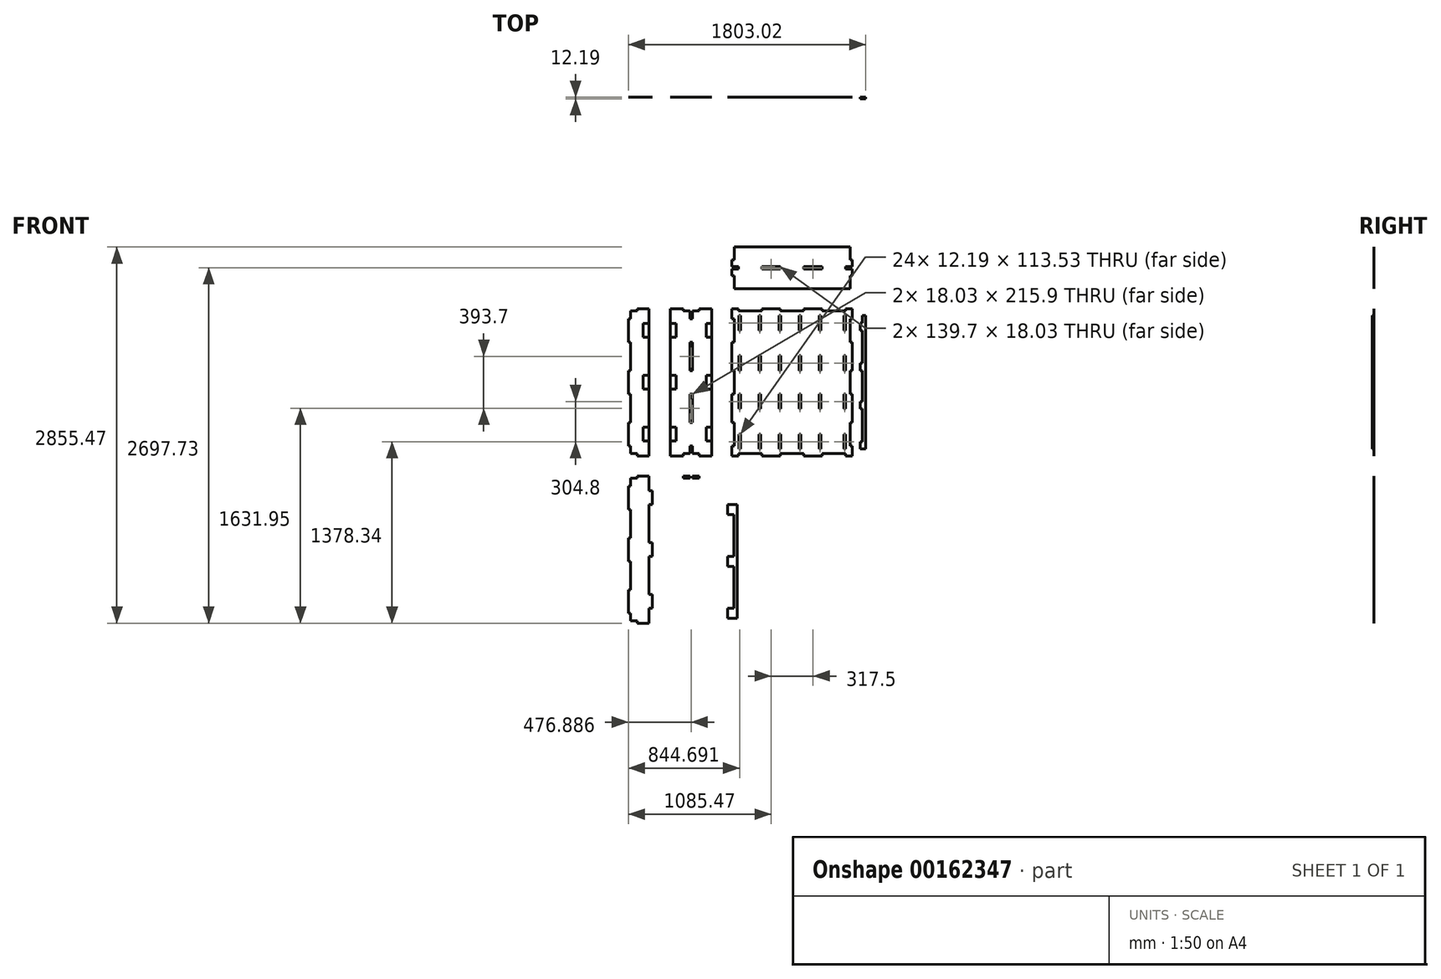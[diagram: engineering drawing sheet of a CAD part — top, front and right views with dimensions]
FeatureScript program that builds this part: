
annotation { "Feature Type Name" : "Feature", "Feature Type Description" : "" }
export const myFeature = defineFeature(function(context is Context, id is Id, definition is map)
    precondition{}
    {
        {
            assignVariable(context, id + "F0", {"name" : "ply34", "anyValue" : 0.71});
        }
        {
            var Q0;
            Q0=qCreatedBy(makeId("Front.planeOp"),FACE);
            var sketch = newSketch(context, id + "F1", { "sketchPlane" : qUnion([Q0])});
            skLineSegment(sketch, "E0.bottom", {"start": v(-457.2, 558.8) * mm, "end": v(457.2, 558.8) * mm});
            skLineSegment(sketch, "E0.top", {"start": v(-457.2, -558.8) * mm, "end": v(457.2, -558.8) * mm});
            skLineSegment(sketch, "E0.left", {"start": v(-457.2, 558.8) * mm, "end": v(-457.2, -558.8) * mm});
            skLineSegment(sketch, "E0.right", {"start": v(457.2, 558.8) * mm, "end": v(457.2, -558.8) * mm});
            skPoint(sketch, "E0.middle", {"position": v(0, 0) * mm});
            skLineSegment(sketch, "E1.bottom", {"start": v(-457.2, 482.6) * mm, "end": v(-439.17, 482.6) * mm});
            skLineSegment(sketch, "E1.top", {"start": v(-457.2, 304.8) * mm, "end": v(-439.17, 304.8) * mm});
            skLineSegment(sketch, "E1.left", {"start": v(-457.2, 482.6) * mm, "end": v(-457.2, 304.8) * mm});
            skLineSegment(sketch, "E1.right", {"start": v(-439.17, 482.6) * mm, "end": v(-439.17, 304.8) * mm});
            skLineSegment(sketch, "E2.bottom", {"start": v(-457.2, 88.9) * mm, "end": v(-439.17, 88.9) * mm});
            skLineSegment(sketch, "E2.top", {"start": v(-457.2, -88.9) * mm, "end": v(-439.17, -88.9) * mm});
            skLineSegment(sketch, "E2.left", {"start": v(-457.2, 88.9) * mm, "end": v(-457.2, -88.9) * mm});
            skLineSegment(sketch, "E2.right", {"start": v(-439.17, 88.9) * mm, "end": v(-439.17, -88.9) * mm});
            skPoint(sketch, "E3", {"position": v(-439.17, 0) * mm});
            skLineSegment(sketch, "E4", {"start": v(-457.2, 0) * mm, "end": v(457.2, 0) * mm, "construction": true});
            skLineSegment(sketch, "E5", {"start": v(0, 558.8) * mm, "end": v(0, -558.8) * mm, "construction": true});
            skLineSegment(sketch, "E6.MirrorCS", {"start": v(-457.2, -482.6) * mm, "end": v(-439.17, -482.6) * mm});
            skLineSegment(sketch, "E7.MirrorCS", {"start": v(-457.2, -304.8) * mm, "end": v(-439.17, -304.8) * mm});
            skLineSegment(sketch, "E8.MirrorCS", {"start": v(-457.2, -482.6) * mm, "end": v(-457.2, -304.8) * mm});
            skLineSegment(sketch, "E9.MirrorCS", {"start": v(-439.17, -482.6) * mm, "end": v(-439.17, -304.8) * mm});
            skLineSegment(sketch, "E10.MirrorCS", {"start": v(457.2, -88.9) * mm, "end": v(439.17, -88.9) * mm});
            skLineSegment(sketch, "E11.MirrorCS", {"start": v(457.2, 304.8) * mm, "end": v(439.17, 304.8) * mm});
            skLineSegment(sketch, "E12.MirrorCS", {"start": v(457.2, 482.6) * mm, "end": v(439.17, 482.6) * mm});
            skLineSegment(sketch, "E13.MirrorCS", {"start": v(457.2, 88.9) * mm, "end": v(439.17, 88.9) * mm});
            skLineSegment(sketch, "E14.MirrorCS", {"start": v(457.2, -304.8) * mm, "end": v(439.17, -304.8) * mm});
            skLineSegment(sketch, "E15.MirrorCS", {"start": v(457.2, -482.6) * mm, "end": v(439.17, -482.6) * mm});
            skLineSegment(sketch, "E16.MirrorCS", {"start": v(439.17, 88.9) * mm, "end": v(439.17, -88.9) * mm});
            skLineSegment(sketch, "E17.MirrorCS", {"start": v(457.2, 88.9) * mm, "end": v(457.2, -88.9) * mm});
            skLineSegment(sketch, "E18.MirrorCS", {"start": v(457.2, -482.6) * mm, "end": v(457.2, -304.8) * mm});
            skLineSegment(sketch, "E19.MirrorCS", {"start": v(439.17, -482.6) * mm, "end": v(439.17, -304.8) * mm});
            skLineSegment(sketch, "E20.MirrorCS", {"start": v(457.2, 482.6) * mm, "end": v(457.2, 304.8) * mm});
            skPoint(sketch, "E21.MirrorP", {"position": v(439.17, 0) * mm});
            skLineSegment(sketch, "E22.MirrorCS", {"start": v(439.17, 482.6) * mm, "end": v(439.17, 304.8) * mm});
            skLineSegment(sketch, "E23.bottom", {"start": v(-406.4, 558.8) * mm, "end": v(-228.6, 558.8) * mm});
            skLineSegment(sketch, "E23.top", {"start": v(-406.4, 540.77) * mm, "end": v(-228.6, 540.77) * mm});
            skLineSegment(sketch, "E23.left", {"start": v(-406.4, 558.8) * mm, "end": v(-406.4, 540.77) * mm});
            skLineSegment(sketch, "E23.right", {"start": v(-228.6, 558.8) * mm, "end": v(-228.6, 540.77) * mm});
            skLineSegment(sketch, "E24.bottom", {"start": v(-88.9, 558.8) * mm, "end": v(88.9, 558.8) * mm});
            skLineSegment(sketch, "E24.top", {"start": v(-88.9, 540.77) * mm, "end": v(88.9, 540.77) * mm});
            skLineSegment(sketch, "E24.left", {"start": v(-88.9, 558.8) * mm, "end": v(-88.9, 540.77) * mm});
            skLineSegment(sketch, "E24.right", {"start": v(88.9, 558.8) * mm, "end": v(88.9, 540.77) * mm});
            skPoint(sketch, "E25", {"position": v(0, 558.8) * mm});
            skLineSegment(sketch, "E26.MirrorCS", {"start": v(228.6, 558.8) * mm, "end": v(228.6, 540.77) * mm});
            skLineSegment(sketch, "E27.MirrorCS", {"start": v(406.4, 558.8) * mm, "end": v(406.4, 540.77) * mm});
            skLineSegment(sketch, "E28.MirrorCS", {"start": v(406.4, 540.77) * mm, "end": v(228.6, 540.77) * mm});
            skLineSegment(sketch, "E29.MirrorCS", {"start": v(406.4, 558.8) * mm, "end": v(228.6, 558.8) * mm});
            skLineSegment(sketch, "E30.MirrorCS", {"start": v(-88.9, -558.8) * mm, "end": v(88.9, -558.8) * mm});
            skLineSegment(sketch, "E31.MirrorCS", {"start": v(228.6, -558.8) * mm, "end": v(228.6, -540.77) * mm});
            skLineSegment(sketch, "E32.MirrorCS", {"start": v(-228.6, -558.8) * mm, "end": v(-228.6, -540.77) * mm});
            skLineSegment(sketch, "E33.MirrorCS", {"start": v(88.9, -558.8) * mm, "end": v(88.9, -540.77) * mm});
            skLineSegment(sketch, "E34.MirrorCS", {"start": v(-406.4, -558.8) * mm, "end": v(-406.4, -540.77) * mm});
            skLineSegment(sketch, "E35.MirrorCS", {"start": v(-88.9, -558.8) * mm, "end": v(-88.9, -540.77) * mm});
            skLineSegment(sketch, "E36.MirrorCS", {"start": v(406.4, -558.8) * mm, "end": v(406.4, -540.77) * mm});
            skLineSegment(sketch, "E37.MirrorCS", {"start": v(-406.4, -558.8) * mm, "end": v(-228.6, -558.8) * mm});
            skLineSegment(sketch, "E38.MirrorCS", {"start": v(-88.9, -540.77) * mm, "end": v(88.9, -540.77) * mm});
            skLineSegment(sketch, "E39.MirrorCS", {"start": v(-406.4, -540.77) * mm, "end": v(-228.6, -540.77) * mm});
            skLineSegment(sketch, "E40.MirrorCS", {"start": v(406.4, -558.8) * mm, "end": v(228.6, -558.8) * mm});
            skLineSegment(sketch, "E41.MirrorCS", {"start": v(406.4, -540.77) * mm, "end": v(228.6, -540.77) * mm});
            skPoint(sketch, "E42.MirrorP", {"position": v(0, -558.8) * mm});
            skLineSegment(sketch, "E43.bottom", {"start": v(-609.6, -558.8) * mm, "end": v(-925.07, -558.8) * mm});
            skLineSegment(sketch, "E43.top", {"start": v(-609.6, 558.8) * mm, "end": v(-925.07, 558.8) * mm});
            skLineSegment(sketch, "E43.left", {"start": v(-609.6, -558.8) * mm, "end": v(-609.6, 558.8) * mm});
            skLineSegment(sketch, "E43.right", {"start": v(-925.07, -558.8) * mm, "end": v(-925.07, 558.8) * mm});
            skLineSegment(sketch, "E44.bottom", {"start": v(-776.35, 558.8) * mm, "end": v(-758.32, 558.8) * mm});
            skLineSegment(sketch, "E44.top", {"start": v(-776.35, 482.6) * mm, "end": v(-758.32, 482.6) * mm});
            skLineSegment(sketch, "E44.left", {"start": v(-776.35, 558.8) * mm, "end": v(-776.35, 482.6) * mm});
            skLineSegment(sketch, "E44.right", {"start": v(-758.32, 558.8) * mm, "end": v(-758.32, 482.6) * mm});
            skPoint(sketch, "E45", {"position": v(-767.33, 558.8) * mm});
            skLineSegment(sketch, "E46.bottom", {"start": v(-776.35, 304.8) * mm, "end": v(-758.32, 304.8) * mm});
            skLineSegment(sketch, "E46.top", {"start": v(-776.35, 88.9) * mm, "end": v(-758.32, 88.9) * mm});
            skLineSegment(sketch, "E46.left", {"start": v(-776.35, 304.8) * mm, "end": v(-776.35, 88.9) * mm});
            skLineSegment(sketch, "E46.right", {"start": v(-758.32, 304.8) * mm, "end": v(-758.32, 88.9) * mm});
            skLineSegment(sketch, "E47.bottom", {"start": v(-776.35, -88.9) * mm, "end": v(-758.32, -88.9) * mm});
            skLineSegment(sketch, "E47.top", {"start": v(-776.35, -304.8) * mm, "end": v(-758.32, -304.8) * mm});
            skLineSegment(sketch, "E47.left", {"start": v(-776.35, -88.9) * mm, "end": v(-776.35, -304.8) * mm});
            skLineSegment(sketch, "E47.right", {"start": v(-758.32, -88.9) * mm, "end": v(-758.32, -304.8) * mm});
            skLineSegment(sketch, "E48.bottom", {"start": v(-776.35, -482.6) * mm, "end": v(-758.32, -482.6) * mm});
            skLineSegment(sketch, "E48.top", {"start": v(-776.35, -558.8) * mm, "end": v(-758.32, -558.8) * mm});
            skLineSegment(sketch, "E48.left", {"start": v(-776.35, -482.6) * mm, "end": v(-776.35, -558.8) * mm});
            skLineSegment(sketch, "E48.right", {"start": v(-758.32, -482.6) * mm, "end": v(-758.32, -558.8) * mm});
            skLineSegment(sketch, "E49.bottom", {"start": v(-776.35, 558.8) * mm, "end": v(-827.15, 558.8) * mm});
            skLineSegment(sketch, "E49.top", {"start": v(-776.35, 540.77) * mm, "end": v(-827.15, 540.77) * mm});
            skLineSegment(sketch, "E49.left", {"start": v(-776.35, 558.8) * mm, "end": v(-776.35, 540.77) * mm});
            skLineSegment(sketch, "E49.right", {"start": v(-827.15, 558.8) * mm, "end": v(-827.15, 540.77) * mm});
            skLineSegment(sketch, "E50.bottom", {"start": v(-758.32, 558.8) * mm, "end": v(-707.52, 558.8) * mm});
            skLineSegment(sketch, "E50.top", {"start": v(-758.32, 540.77) * mm, "end": v(-707.52, 540.77) * mm});
            skLineSegment(sketch, "E50.left", {"start": v(-758.32, 558.8) * mm, "end": v(-758.32, 540.77) * mm});
            skLineSegment(sketch, "E50.right", {"start": v(-707.52, 558.8) * mm, "end": v(-707.52, 540.77) * mm});
            skLineSegment(sketch, "E51.MirrorCS", {"start": v(-758.32, -540.77) * mm, "end": v(-707.52, -540.77) * mm});
            skLineSegment(sketch, "E52.MirrorCS", {"start": v(-758.32, -558.8) * mm, "end": v(-707.52, -558.8) * mm});
            skLineSegment(sketch, "E53.MirrorCS", {"start": v(-758.32, -558.8) * mm, "end": v(-758.32, -540.77) * mm});
            skLineSegment(sketch, "E54.MirrorCS", {"start": v(-827.15, -558.8) * mm, "end": v(-827.15, -540.77) * mm});
            skLineSegment(sketch, "E55.MirrorCS", {"start": v(-776.35, -540.77) * mm, "end": v(-827.15, -540.77) * mm});
            skPoint(sketch, "E56.MirrorP", {"position": v(-767.33, -558.8) * mm});
            skLineSegment(sketch, "E57.MirrorCS", {"start": v(-776.35, -558.8) * mm, "end": v(-776.35, -540.77) * mm});
            skLineSegment(sketch, "E58.MirrorCS", {"start": v(-776.35, -558.8) * mm, "end": v(-827.15, -558.8) * mm});
            skLineSegment(sketch, "E59.MirrorCS", {"start": v(-707.52, -558.8) * mm, "end": v(-707.52, -540.77) * mm});
            skLineSegment(sketch, "E60.bottom", {"start": v(-439.17, 1026.67) * mm, "end": v(439.17, 1026.67) * mm});
            skLineSegment(sketch, "E60.top", {"start": v(-439.17, 711.2) * mm, "end": v(439.17, 711.2) * mm});
            skLineSegment(sketch, "E60.left", {"start": v(-439.17, 1026.67) * mm, "end": v(-439.17, 711.2) * mm});
            skLineSegment(sketch, "E60.right", {"start": v(439.17, 1026.67) * mm, "end": v(439.17, 711.2) * mm});
            skLineSegment(sketch, "E61.bottom", {"start": v(-439.17, 877.95) * mm, "end": v(-457.2, 877.95) * mm});
            skLineSegment(sketch, "E61.top", {"start": v(-439.17, 928.75) * mm, "end": v(-457.2, 928.75) * mm});
            skLineSegment(sketch, "E61.left", {"start": v(-439.17, 877.95) * mm, "end": v(-439.17, 928.75) * mm});
            skLineSegment(sketch, "E61.right", {"start": v(-457.2, 877.95) * mm, "end": v(-457.2, 928.75) * mm});
            skLineSegment(sketch, "E62.bottom", {"start": v(-439.17, 859.92) * mm, "end": v(-457.2, 859.92) * mm});
            skLineSegment(sketch, "E62.top", {"start": v(-439.17, 809.12) * mm, "end": v(-457.2, 809.12) * mm});
            skLineSegment(sketch, "E62.left", {"start": v(-439.17, 859.92) * mm, "end": v(-439.17, 809.12) * mm});
            skLineSegment(sketch, "E62.right", {"start": v(-457.2, 859.92) * mm, "end": v(-457.2, 809.12) * mm});
            skLineSegment(sketch, "E63", {"start": v(-448.18, 877.95) * mm, "end": v(-448.18, 859.92) * mm, "construction": true});
            skPoint(sketch, "E64", {"position": v(-448.18, 868.93) * mm});
            skPoint(sketch, "E65", {"position": v(-439.17, 868.93) * mm});
            skLineSegment(sketch, "E66.bottom", {"start": v(-439.17, 877.95) * mm, "end": v(-406.4, 877.95) * mm});
            skLineSegment(sketch, "E66.top", {"start": v(-439.17, 859.92) * mm, "end": v(-406.4, 859.92) * mm});
            skLineSegment(sketch, "E66.left", {"start": v(-439.17, 877.95) * mm, "end": v(-439.17, 859.92) * mm});
            skLineSegment(sketch, "E66.right", {"start": v(-406.4, 877.95) * mm, "end": v(-406.4, 859.92) * mm});
            skLineSegment(sketch, "E67.bottom", {"start": v(-228.6, 877.95) * mm, "end": v(-88.9, 877.95) * mm});
            skLineSegment(sketch, "E67.top", {"start": v(-228.6, 859.92) * mm, "end": v(-88.9, 859.92) * mm});
            skLineSegment(sketch, "E67.left", {"start": v(-228.6, 877.95) * mm, "end": v(-228.6, 859.92) * mm});
            skLineSegment(sketch, "E67.right", {"start": v(-88.9, 877.95) * mm, "end": v(-88.9, 859.92) * mm});
            skLineSegment(sketch, "E68.bottom", {"start": v(88.9, 877.95) * mm, "end": v(228.6, 877.95) * mm});
            skLineSegment(sketch, "E68.top", {"start": v(88.9, 859.92) * mm, "end": v(228.6, 859.92) * mm});
            skLineSegment(sketch, "E68.left", {"start": v(88.9, 877.95) * mm, "end": v(88.9, 859.92) * mm});
            skLineSegment(sketch, "E68.right", {"start": v(228.6, 877.95) * mm, "end": v(228.6, 859.92) * mm});
            skLineSegment(sketch, "E69.MirrorCS", {"start": v(439.17, 877.95) * mm, "end": v(439.17, 859.92) * mm});
            skLineSegment(sketch, "E70.MirrorCS", {"start": v(439.17, 877.95) * mm, "end": v(457.2, 877.95) * mm});
            skLineSegment(sketch, "E71.MirrorCS", {"start": v(406.4, 877.95) * mm, "end": v(406.4, 859.92) * mm});
            skLineSegment(sketch, "E72.MirrorCS", {"start": v(439.17, 928.75) * mm, "end": v(457.2, 928.75) * mm});
            skLineSegment(sketch, "E73.MirrorCS", {"start": v(448.18, 877.95) * mm, "end": v(448.18, 859.92) * mm, "construction": true});
            skLineSegment(sketch, "E74.MirrorCS", {"start": v(439.17, 809.12) * mm, "end": v(457.2, 809.12) * mm});
            skLineSegment(sketch, "E75.MirrorCS", {"start": v(439.17, 859.92) * mm, "end": v(457.2, 859.92) * mm});
            skLineSegment(sketch, "E76.MirrorCS", {"start": v(439.17, 877.95) * mm, "end": v(406.4, 877.95) * mm});
            skLineSegment(sketch, "E77.MirrorCS", {"start": v(439.17, 859.92) * mm, "end": v(406.4, 859.92) * mm});
            skLineSegment(sketch, "E78.MirrorCS", {"start": v(439.17, 877.95) * mm, "end": v(439.17, 928.75) * mm});
            skLineSegment(sketch, "E79.MirrorCS", {"start": v(439.17, 859.92) * mm, "end": v(439.17, 809.12) * mm});
            skLineSegment(sketch, "E80.MirrorCS", {"start": v(457.2, 877.95) * mm, "end": v(457.2, 928.75) * mm});
            skPoint(sketch, "E81.MirrorP", {"position": v(439.17, 868.93) * mm});
            skLineSegment(sketch, "E82.MirrorCS", {"start": v(457.2, 859.92) * mm, "end": v(457.2, 809.12) * mm});
            skPoint(sketch, "E83.MirrorP", {"position": v(448.18, 868.93) * mm});
            skLineSegment(sketch, "E84", {"start": v(-767.33, -558.8) * mm, "end": v(-767.33, 558.8) * mm, "construction": true});
            skLineSegment(sketch, "E85", {"start": v(439.17, 1102.87) * mm, "end": v(-439.17, 1102.87) * mm, "construction": true});
            skLineSegment(sketch, "E86.MirrorCS", {"start": v(228.6, 1327.78) * mm, "end": v(228.6, 1345.82) * mm});
            skLineSegment(sketch, "E87.MirrorCS", {"start": v(-228.6, 1327.78) * mm, "end": v(-228.6, 1345.82) * mm});
            skLineSegment(sketch, "E88.MirrorCS", {"start": v(-88.9, 1327.78) * mm, "end": v(-88.9, 1345.82) * mm});
            skLineSegment(sketch, "E89.MirrorCS", {"start": v(88.9, 1327.78) * mm, "end": v(88.9, 1345.82) * mm});
            skLineSegment(sketch, "E90.MirrorCS", {"start": v(-228.6, 1345.82) * mm, "end": v(-88.9, 1345.82) * mm});
            skLineSegment(sketch, "E91.MirrorCS", {"start": v(-228.6, 1327.78) * mm, "end": v(-88.9, 1327.78) * mm});
            skLineSegment(sketch, "E92.MirrorCS", {"start": v(88.9, 1345.82) * mm, "end": v(228.6, 1345.82) * mm});
            skLineSegment(sketch, "E93.MirrorCS", {"start": v(88.9, 1327.78) * mm, "end": v(228.6, 1327.78) * mm});
            skLineSegment(sketch, "E94.MirrorCS", {"start": v(439.17, 1276.98) * mm, "end": v(457.2, 1276.98) * mm});
            skLineSegment(sketch, "E95.MirrorCS", {"start": v(457.2, 1327.78) * mm, "end": v(457.2, 1276.98) * mm});
            skLineSegment(sketch, "E96.MirrorCS", {"start": v(439.17, 1327.78) * mm, "end": v(457.2, 1327.78) * mm});
            skLineSegment(sketch, "E97.MirrorCS", {"start": v(439.17, 1327.78) * mm, "end": v(406.4, 1327.78) * mm});
            skLineSegment(sketch, "E98.MirrorCS", {"start": v(406.4, 1327.78) * mm, "end": v(406.4, 1345.82) * mm});
            skLineSegment(sketch, "E99.MirrorCS", {"start": v(439.17, 1345.82) * mm, "end": v(406.4, 1345.82) * mm});
            skLineSegment(sketch, "E100.MirrorCS", {"start": v(-439.17, 1276.98) * mm, "end": v(-457.2, 1276.98) * mm});
            skLineSegment(sketch, "E101.MirrorCS", {"start": v(-457.2, 1327.78) * mm, "end": v(-457.2, 1276.98) * mm});
            skLineSegment(sketch, "E102.MirrorCS", {"start": v(-439.17, 1327.78) * mm, "end": v(-457.2, 1327.78) * mm});
            skLineSegment(sketch, "E103.MirrorCS", {"start": v(-439.17, 1327.78) * mm, "end": v(-406.4, 1327.78) * mm});
            skLineSegment(sketch, "E104.MirrorCS", {"start": v(-406.4, 1327.78) * mm, "end": v(-406.4, 1345.82) * mm});
            skLineSegment(sketch, "E105.MirrorCS", {"start": v(-439.17, 1345.82) * mm, "end": v(-406.4, 1345.82) * mm});
            skLineSegment(sketch, "E106", {"start": v(-406.4, 1345.82) * mm, "end": v(-228.6, 1345.82) * mm});
            skLineSegment(sketch, "E107", {"start": v(-88.9, 1345.82) * mm, "end": v(88.9, 1345.82) * mm});
            skLineSegment(sketch, "E108", {"start": v(228.6, 1345.82) * mm, "end": v(406.4, 1345.82) * mm});
            skLineSegment(sketch, "E109.bottom", {"start": v(-609.6, 52.07) * mm, "end": v(-653.31, 52.07) * mm});
            skLineSegment(sketch, "E109.top", {"start": v(-609.6, -52.07) * mm, "end": v(-653.31, -52.07) * mm});
            skLineSegment(sketch, "E109.left", {"start": v(-609.6, 52.07) * mm, "end": v(-609.6, -52.07) * mm});
            skLineSegment(sketch, "E109.right", {"start": v(-653.31, 52.07) * mm, "end": v(-653.31, -52.07) * mm});
            skPoint(sketch, "E110", {"position": v(-609.6, 0) * mm});
            skLineSegment(sketch, "E111", {"start": v(-758.32, 482.6) * mm, "end": v(-758.32, 304.8) * mm, "construction": true});
            skLineSegment(sketch, "E112.bottom", {"start": v(-653.31, 341.63) * mm, "end": v(-609.6, 341.63) * mm});
            skLineSegment(sketch, "E112.top", {"start": v(-653.31, 445.77) * mm, "end": v(-609.6, 445.77) * mm});
            skLineSegment(sketch, "E112.left", {"start": v(-653.31, 341.63) * mm, "end": v(-653.31, 445.77) * mm});
            skLineSegment(sketch, "E112.right", {"start": v(-609.6, 341.63) * mm, "end": v(-609.6, 445.77) * mm});
            skPoint(sketch, "E112.middle", {"position": v(-631.46, 393.7) * mm});
            skPoint(sketch, "E112.middle.positionSnap0", {"position": v(-631.46, 52.07) * mm});
            skPoint(sketch, "E112.middle.positionSnap1", {"position": v(-758.32, 393.7) * mm});
            skPoint(sketch, "E112.centerSnap0", {"position": v(-631.46, 52.07) * mm});
            skPoint(sketch, "E112.centerSnap1", {"position": v(-758.32, 393.7) * mm});
            skLineSegment(sketch, "E113.MirrorCS", {"start": v(-653.31, -341.63) * mm, "end": v(-609.6, -341.63) * mm});
            skLineSegment(sketch, "E114.MirrorCS", {"start": v(-653.31, -445.77) * mm, "end": v(-609.6, -445.77) * mm});
            skLineSegment(sketch, "E115.MirrorCS", {"start": v(-653.31, -341.63) * mm, "end": v(-653.31, -445.77) * mm});
            skPoint(sketch, "E116.MirrorP", {"position": v(-631.46, -393.7) * mm});
            skLineSegment(sketch, "E117.MirrorCS", {"start": v(-609.6, -341.63) * mm, "end": v(-609.6, -445.77) * mm});
            skLineSegment(sketch, "E118.MirrorCS", {"start": v(-881.35, -445.77) * mm, "end": v(-925.07, -445.77) * mm});
            skLineSegment(sketch, "E119.MirrorCS", {"start": v(-881.35, -341.63) * mm, "end": v(-925.07, -341.63) * mm});
            skLineSegment(sketch, "E120.MirrorCS", {"start": v(-881.35, 445.77) * mm, "end": v(-925.07, 445.77) * mm});
            skLineSegment(sketch, "E121.MirrorCS", {"start": v(-881.35, 341.63) * mm, "end": v(-925.07, 341.63) * mm});
            skLineSegment(sketch, "E122.MirrorCS", {"start": v(-925.07, -52.07) * mm, "end": v(-881.35, -52.07) * mm});
            skLineSegment(sketch, "E123.MirrorCS", {"start": v(-925.07, 52.07) * mm, "end": v(-881.35, 52.07) * mm});
            skLineSegment(sketch, "E124.MirrorCS", {"start": v(-925.07, -341.63) * mm, "end": v(-925.07, -445.77) * mm});
            skPoint(sketch, "E125.MirrorP", {"position": v(-903.21, 52.07) * mm});
            skLineSegment(sketch, "E126.MirrorCS", {"start": v(-881.35, -341.63) * mm, "end": v(-881.35, -445.77) * mm});
            skLineSegment(sketch, "E127.MirrorCS", {"start": v(-925.07, 341.63) * mm, "end": v(-925.07, 445.77) * mm});
            skLineSegment(sketch, "E128.MirrorCS", {"start": v(-881.35, 341.63) * mm, "end": v(-881.35, 445.77) * mm});
            skLineSegment(sketch, "E129.MirrorCS", {"start": v(-925.07, 52.07) * mm, "end": v(-925.07, -52.07) * mm});
            skLineSegment(sketch, "E130.MirrorCS", {"start": v(-881.35, 52.07) * mm, "end": v(-881.35, -52.07) * mm});
            skPoint(sketch, "E131.MirrorP", {"position": v(-903.21, 393.7) * mm});
            skPoint(sketch, "E132.MirrorP", {"position": v(-925.07, 0) * mm});
            skPoint(sketch, "E133.MirrorP", {"position": v(-903.21, -393.7) * mm});
            skLineSegment(sketch, "E134.bottom", {"start": v(-405.63, 507.23) * mm, "end": v(405.63, 507.23) * mm, "construction": true});
            skLineSegment(sketch, "E134.top", {"start": v(-405.63, -507.23) * mm, "end": v(405.63, -507.23) * mm, "construction": true});
            skLineSegment(sketch, "E134.left", {"start": v(-405.63, 507.23) * mm, "end": v(-405.63, -507.23) * mm, "construction": true});
            skLineSegment(sketch, "E134.right", {"start": v(405.63, 507.23) * mm, "end": v(405.63, -507.23) * mm, "construction": true});
            skLineSegment(sketch, "E135.0", {"start": v(-393.43, 495.03) * mm, "end": v(393.43, 495.03) * mm, "construction": true});
            skLineSegment(sketch, "E135.1", {"start": v(-393.43, 495.03) * mm, "end": v(-393.43, -495.03) * mm, "construction": true});
            skLineSegment(sketch, "E135.2", {"start": v(-393.43, -495.03) * mm, "end": v(393.43, -495.03) * mm, "construction": true});
            skLineSegment(sketch, "E135.3", {"start": v(393.43, 495.03) * mm, "end": v(393.43, -495.03) * mm, "construction": true});
            skPoint(sketch, "E136.oppositeSnap0", {"position": v(-439.17, 393.7) * mm});
            skLineSegment(sketch, "E136.bottom", {"start": v(-405.63, 507.23) * mm, "end": v(-393.43, 507.23) * mm});
            skLineSegment(sketch, "E136.top", {"start": v(-405.63, 393.7) * mm, "end": v(-393.43, 393.7) * mm});
            skLineSegment(sketch, "E136.left", {"start": v(-405.63, 507.23) * mm, "end": v(-405.63, 393.7) * mm});
            skLineSegment(sketch, "E136.right", {"start": v(-393.43, 507.23) * mm, "end": v(-393.43, 393.7) * mm});
            skPoint(sketch, "E137.oppositeSnap0", {"position": v(-439.17, -393.7) * mm});
            skLineSegment(sketch, "E137.bottom", {"start": v(-405.63, -507.23) * mm, "end": v(-393.43, -507.23) * mm});
            skLineSegment(sketch, "E137.top", {"start": v(-405.63, -393.7) * mm, "end": v(-393.43, -393.7) * mm});
            skLineSegment(sketch, "E137.left", {"start": v(-405.63, -507.23) * mm, "end": v(-405.63, -393.7) * mm});
            skLineSegment(sketch, "E137.right", {"start": v(-393.43, -507.23) * mm, "end": v(-393.43, -393.7) * mm});
            skLineSegment(sketch, "E138.bottom", {"start": v(-405.63, 88.9) * mm, "end": v(-393.43, 88.9) * mm});
            skLineSegment(sketch, "E138.top", {"start": v(-405.63, 202.43) * mm, "end": v(-393.43, 202.43) * mm});
            skLineSegment(sketch, "E138.left", {"start": v(-405.63, 88.9) * mm, "end": v(-405.63, 202.43) * mm});
            skLineSegment(sketch, "E138.right", {"start": v(-393.43, 88.9) * mm, "end": v(-393.43, 202.43) * mm});
            skLineSegment(sketch, "E139.bottom", {"start": v(-405.63, -88.9) * mm, "end": v(-393.43, -88.9) * mm});
            skLineSegment(sketch, "E139.top", {"start": v(-405.63, -202.43) * mm, "end": v(-393.43, -202.43) * mm});
            skLineSegment(sketch, "E139.left", {"start": v(-405.63, -88.9) * mm, "end": v(-405.63, -202.43) * mm});
            skLineSegment(sketch, "E139.right", {"start": v(-393.43, -88.9) * mm, "end": v(-393.43, -202.43) * mm});
            skLineSegment(sketch, "E140.1.0.0", {"start": v(-253.23, -507.23) * mm, "end": v(-253.23, -393.7) * mm});
            skLineSegment(sketch, "E140.1.0.1", {"start": v(-241.03, -507.23) * mm, "end": v(-241.03, -393.7) * mm});
            skLineSegment(sketch, "E140.1.0.2", {"start": v(-253.23, -507.23) * mm, "end": v(-241.03, -507.23) * mm});
            skLineSegment(sketch, "E140.1.0.3", {"start": v(-253.23, -393.7) * mm, "end": v(-241.03, -393.7) * mm});
            skLineSegment(sketch, "E140.1.0.4", {"start": v(-253.23, -88.9) * mm, "end": v(-241.03, -88.9) * mm});
            skLineSegment(sketch, "E140.1.0.5", {"start": v(-253.23, -202.43) * mm, "end": v(-241.03, -202.43) * mm});
            skLineSegment(sketch, "E140.1.0.6", {"start": v(-253.23, -88.9) * mm, "end": v(-253.23, -202.43) * mm});
            skLineSegment(sketch, "E140.1.0.7", {"start": v(-241.03, -88.9) * mm, "end": v(-241.03, -202.43) * mm});
            skLineSegment(sketch, "E140.1.0.8", {"start": v(-253.23, 88.9) * mm, "end": v(-253.23, 202.43) * mm});
            skLineSegment(sketch, "E140.1.0.9", {"start": v(-241.03, 88.9) * mm, "end": v(-241.03, 202.43) * mm});
            skLineSegment(sketch, "E140.1.0.10", {"start": v(-253.23, 88.9) * mm, "end": v(-241.03, 88.9) * mm});
            skLineSegment(sketch, "E140.1.0.11", {"start": v(-253.23, 202.43) * mm, "end": v(-241.03, 202.43) * mm});
            skLineSegment(sketch, "E140.1.0.12", {"start": v(-253.23, 507.23) * mm, "end": v(-241.03, 507.23) * mm});
            skLineSegment(sketch, "E140.1.0.13", {"start": v(-253.23, 393.7) * mm, "end": v(-241.03, 393.7) * mm});
            skLineSegment(sketch, "E140.1.0.14", {"start": v(-253.23, 507.23) * mm, "end": v(-253.23, 393.7) * mm});
            skLineSegment(sketch, "E140.1.0.15", {"start": v(-241.03, 507.23) * mm, "end": v(-241.03, 393.7) * mm});
            skLineSegment(sketch, "E140.2.0.0", {"start": v(-100.83, -507.23) * mm, "end": v(-100.83, -393.7) * mm});
            skLineSegment(sketch, "E140.2.0.1", {"start": v(-88.63, -507.23) * mm, "end": v(-88.63, -393.7) * mm});
            skLineSegment(sketch, "E140.2.0.2", {"start": v(-100.83, -507.23) * mm, "end": v(-88.63, -507.23) * mm});
            skLineSegment(sketch, "E140.2.0.3", {"start": v(-100.83, -393.7) * mm, "end": v(-88.63, -393.7) * mm});
            skLineSegment(sketch, "E140.2.0.4", {"start": v(-100.83, -88.9) * mm, "end": v(-88.63, -88.9) * mm});
            skLineSegment(sketch, "E140.2.0.5", {"start": v(-100.83, -202.43) * mm, "end": v(-88.63, -202.43) * mm});
            skLineSegment(sketch, "E140.2.0.6", {"start": v(-100.83, -88.9) * mm, "end": v(-100.83, -202.43) * mm});
            skLineSegment(sketch, "E140.2.0.7", {"start": v(-88.63, -88.9) * mm, "end": v(-88.63, -202.43) * mm});
            skLineSegment(sketch, "E140.2.0.8", {"start": v(-100.83, 88.9) * mm, "end": v(-100.83, 202.43) * mm});
            skLineSegment(sketch, "E140.2.0.9", {"start": v(-88.63, 88.9) * mm, "end": v(-88.63, 202.43) * mm});
            skLineSegment(sketch, "E140.2.0.10", {"start": v(-100.83, 88.9) * mm, "end": v(-88.63, 88.9) * mm});
            skLineSegment(sketch, "E140.2.0.11", {"start": v(-100.83, 202.43) * mm, "end": v(-88.63, 202.43) * mm});
            skLineSegment(sketch, "E140.2.0.12", {"start": v(-100.83, 507.23) * mm, "end": v(-88.63, 507.23) * mm});
            skLineSegment(sketch, "E140.2.0.13", {"start": v(-100.83, 393.7) * mm, "end": v(-88.63, 393.7) * mm});
            skLineSegment(sketch, "E140.2.0.14", {"start": v(-100.83, 507.23) * mm, "end": v(-100.83, 393.7) * mm});
            skLineSegment(sketch, "E140.2.0.15", {"start": v(-88.63, 507.23) * mm, "end": v(-88.63, 393.7) * mm});
            skLineSegment(sketch, "E140.3.0.0", {"start": v(51.57, -507.23) * mm, "end": v(51.57, -393.7) * mm});
            skLineSegment(sketch, "E140.3.0.1", {"start": v(63.77, -507.23) * mm, "end": v(63.77, -393.7) * mm});
            skLineSegment(sketch, "E140.3.0.2", {"start": v(51.57, -507.23) * mm, "end": v(63.77, -507.23) * mm});
            skLineSegment(sketch, "E140.3.0.3", {"start": v(51.57, -393.7) * mm, "end": v(63.77, -393.7) * mm});
            skLineSegment(sketch, "E140.3.0.4", {"start": v(51.57, -88.9) * mm, "end": v(63.77, -88.9) * mm});
            skLineSegment(sketch, "E140.3.0.5", {"start": v(51.57, -202.43) * mm, "end": v(63.77, -202.43) * mm});
            skLineSegment(sketch, "E140.3.0.6", {"start": v(51.57, -88.9) * mm, "end": v(51.57, -202.43) * mm});
            skLineSegment(sketch, "E140.3.0.7", {"start": v(63.77, -88.9) * mm, "end": v(63.77, -202.43) * mm});
            skLineSegment(sketch, "E140.3.0.8", {"start": v(51.57, 88.9) * mm, "end": v(51.57, 202.43) * mm});
            skLineSegment(sketch, "E140.3.0.9", {"start": v(63.77, 88.9) * mm, "end": v(63.77, 202.43) * mm});
            skLineSegment(sketch, "E140.3.0.10", {"start": v(51.57, 88.9) * mm, "end": v(63.77, 88.9) * mm});
            skLineSegment(sketch, "E140.3.0.11", {"start": v(51.57, 202.43) * mm, "end": v(63.77, 202.43) * mm});
            skLineSegment(sketch, "E140.3.0.12", {"start": v(51.57, 507.23) * mm, "end": v(63.77, 507.23) * mm});
            skLineSegment(sketch, "E140.3.0.13", {"start": v(51.57, 393.7) * mm, "end": v(63.77, 393.7) * mm});
            skLineSegment(sketch, "E140.3.0.14", {"start": v(51.57, 507.23) * mm, "end": v(51.57, 393.7) * mm});
            skLineSegment(sketch, "E140.3.0.15", {"start": v(63.77, 507.23) * mm, "end": v(63.77, 393.7) * mm});
            skLineSegment(sketch, "E140.4.0.0", {"start": v(203.97, -507.23) * mm, "end": v(203.97, -393.7) * mm});
            skLineSegment(sketch, "E140.4.0.1", {"start": v(216.17, -507.23) * mm, "end": v(216.17, -393.7) * mm});
            skLineSegment(sketch, "E140.4.0.2", {"start": v(203.97, -507.23) * mm, "end": v(216.17, -507.23) * mm});
            skLineSegment(sketch, "E140.4.0.3", {"start": v(203.97, -393.7) * mm, "end": v(216.17, -393.7) * mm});
            skLineSegment(sketch, "E140.4.0.4", {"start": v(203.97, -88.9) * mm, "end": v(216.17, -88.9) * mm});
            skLineSegment(sketch, "E140.4.0.5", {"start": v(203.97, -202.43) * mm, "end": v(216.17, -202.43) * mm});
            skLineSegment(sketch, "E140.4.0.6", {"start": v(203.97, -88.9) * mm, "end": v(203.97, -202.43) * mm});
            skLineSegment(sketch, "E140.4.0.7", {"start": v(216.17, -88.9) * mm, "end": v(216.17, -202.43) * mm});
            skLineSegment(sketch, "E140.4.0.8", {"start": v(203.97, 88.9) * mm, "end": v(203.97, 202.43) * mm});
            skLineSegment(sketch, "E140.4.0.9", {"start": v(216.17, 88.9) * mm, "end": v(216.17, 202.43) * mm});
            skLineSegment(sketch, "E140.4.0.10", {"start": v(203.97, 88.9) * mm, "end": v(216.17, 88.9) * mm});
            skLineSegment(sketch, "E140.4.0.11", {"start": v(203.97, 202.43) * mm, "end": v(216.17, 202.43) * mm});
            skLineSegment(sketch, "E140.4.0.12", {"start": v(203.97, 507.23) * mm, "end": v(216.17, 507.23) * mm});
            skLineSegment(sketch, "E140.4.0.13", {"start": v(203.97, 393.7) * mm, "end": v(216.17, 393.7) * mm});
            skLineSegment(sketch, "E140.4.0.14", {"start": v(203.97, 507.23) * mm, "end": v(203.97, 393.7) * mm});
            skLineSegment(sketch, "E140.4.0.15", {"start": v(216.17, 507.23) * mm, "end": v(216.17, 393.7) * mm});
            skLineSegment(sketch, "E140.direction1", {"start": v(-405.63, -507.23) * mm, "end": v(-253.23, -507.23) * mm, "construction": true});
            skLineSegment(sketch, "E141.MirrorCS", {"start": v(405.63, 507.23) * mm, "end": v(393.43, 507.23) * mm});
            skLineSegment(sketch, "E142.MirrorCS", {"start": v(405.63, 393.7) * mm, "end": v(393.43, 393.7) * mm});
            skLineSegment(sketch, "E143.MirrorCS", {"start": v(405.63, 507.23) * mm, "end": v(405.63, 393.7) * mm});
            skLineSegment(sketch, "E144.MirrorCS", {"start": v(393.43, 507.23) * mm, "end": v(393.43, 393.7) * mm});
            skLineSegment(sketch, "E145.MirrorCS", {"start": v(405.63, -202.43) * mm, "end": v(393.43, -202.43) * mm});
            skLineSegment(sketch, "E146.MirrorCS", {"start": v(405.63, -88.9) * mm, "end": v(393.43, -88.9) * mm});
            skLineSegment(sketch, "E147.MirrorCS", {"start": v(405.63, 88.9) * mm, "end": v(393.43, 88.9) * mm});
            skLineSegment(sketch, "E148.MirrorCS", {"start": v(405.63, 202.43) * mm, "end": v(393.43, 202.43) * mm});
            skLineSegment(sketch, "E149.MirrorCS", {"start": v(393.43, 88.9) * mm, "end": v(393.43, 202.43) * mm});
            skLineSegment(sketch, "E150.MirrorCS", {"start": v(393.43, -88.9) * mm, "end": v(393.43, -202.43) * mm});
            skLineSegment(sketch, "E151.MirrorCS", {"start": v(405.63, -88.9) * mm, "end": v(405.63, -202.43) * mm});
            skLineSegment(sketch, "E152.MirrorCS", {"start": v(405.63, 88.9) * mm, "end": v(405.63, 202.43) * mm});
            skLineSegment(sketch, "E153.MirrorCS", {"start": v(393.43, -507.23) * mm, "end": v(393.43, -393.7) * mm});
            skLineSegment(sketch, "E154.MirrorCS", {"start": v(405.63, -507.23) * mm, "end": v(405.63, -393.7) * mm});
            skLineSegment(sketch, "E155.MirrorCS", {"start": v(405.63, -507.23) * mm, "end": v(393.43, -507.23) * mm});
            skLineSegment(sketch, "E156.MirrorCS", {"start": v(405.63, -393.7) * mm, "end": v(393.43, -393.7) * mm});
            skLineSegment(sketch, "E157.bottom", {"start": v(533.4, 507.23) * mm, "end": v(558.8, 507.23) * mm});
            skLineSegment(sketch, "E157.top", {"start": v(533.4, -507.23) * mm, "end": v(558.8, -507.23) * mm});
            skLineSegment(sketch, "E157.left", {"start": v(533.4, 507.23) * mm, "end": v(533.4, -507.23) * mm});
            skLineSegment(sketch, "E157.right", {"start": v(558.8, 507.23) * mm, "end": v(558.8, -507.23) * mm});
            skPoint(sketch, "E158.startSnap0", {"position": v(405.63, 450.46) * mm});
            skPoint(sketch, "E159.endSnap0", {"position": v(533.4, 0) * mm});
            skLineSegment(sketch, "E160", {"start": v(533.4, 88.9) * mm, "end": v(515.37, 88.9) * mm});
            skLineSegment(sketch, "E161", {"start": v(515.37, 88.9) * mm, "end": v(515.37, 145.66) * mm});
            skPoint(sketch, "E161.endSnap0", {"position": v(405.63, 145.66) * mm});
            skLineSegment(sketch, "E162", {"start": v(533.4, 145.66) * mm, "end": v(515.37, 145.66) * mm});
            skLineSegment(sketch, "E163", {"start": v(533.4, 393.7) * mm, "end": v(515.37, 393.7) * mm});
            skPoint(sketch, "E163.startSnap0", {"position": v(457.2, 393.7) * mm});
            skLineSegment(sketch, "E164", {"start": v(515.37, 393.7) * mm, "end": v(515.37, 450.46) * mm});
            skLineSegment(sketch, "E165", {"start": v(533.4, 450.46) * mm, "end": v(515.37, 450.46) * mm});
            skLineSegment(sketch, "E166", {"start": v(533.4, -202.43) * mm, "end": v(515.37, -202.43) * mm});
            skLineSegment(sketch, "E167", {"start": v(515.37, -202.43) * mm, "end": v(515.37, -145.66) * mm});
            skPoint(sketch, "E167.endSnap0", {"position": v(405.63, -145.66) * mm});
            skLineSegment(sketch, "E168", {"start": v(533.4, -145.66) * mm, "end": v(515.37, -145.66) * mm});
            skLineSegment(sketch, "E169", {"start": v(533.4, -507.23) * mm, "end": v(515.37, -507.23) * mm});
            skLineSegment(sketch, "E170", {"start": v(515.37, -507.23) * mm, "end": v(515.37, -450.46) * mm});
            skPoint(sketch, "E171", {"position": v(405.63, -450.46) * mm});
            skLineSegment(sketch, "E172", {"start": v(533.4, -450.46) * mm, "end": v(515.37, -450.46) * mm});
            skLineSegment(sketch, "E173.bottom", {"start": v(-940.94, -711.2) * mm, "end": v(-593.72, -711.2) * mm});
            skLineSegment(sketch, "E173.top", {"start": v(-940.94, -1828.8) * mm, "end": v(-593.72, -1828.8) * mm});
            skLineSegment(sketch, "E173.left", {"start": v(-940.94, -711.2) * mm, "end": v(-940.94, -1828.8) * mm});
            skLineSegment(sketch, "E173.right", {"start": v(-593.72, -711.2) * mm, "end": v(-593.72, -1828.8) * mm});
            skPoint(sketch, "E174", {"position": v(-767.33, -711.2) * mm});
            skLineSegment(sketch, "E175", {"start": v(-925.07, -635) * mm, "end": v(-703.26, -635) * mm, "construction": true});
            skLineSegment(sketch, "E176.MirrorCS", {"start": v(-881.35, -1715.77) * mm, "end": v(-925.07, -1715.77) * mm, "construction": true});
            skLineSegment(sketch, "E177.MirrorCS", {"start": v(-881.35, -1611.63) * mm, "end": v(-925.07, -1611.63) * mm, "construction": true});
            skLineSegment(sketch, "E178.MirrorCS", {"start": v(-653.31, -1611.63) * mm, "end": v(-609.6, -1611.63) * mm, "construction": true});
            skLineSegment(sketch, "E179.MirrorCS", {"start": v(-653.31, -1715.77) * mm, "end": v(-609.6, -1715.77) * mm, "construction": true});
            skLineSegment(sketch, "E180.MirrorCS", {"start": v(-609.6, -1322.07) * mm, "end": v(-653.31, -1322.07) * mm, "construction": true});
            skLineSegment(sketch, "E181.MirrorCS", {"start": v(-925.07, -1322.07) * mm, "end": v(-881.35, -1322.07) * mm, "construction": true});
            skLineSegment(sketch, "E182.MirrorCS", {"start": v(-925.07, -1217.93) * mm, "end": v(-881.35, -1217.93) * mm, "construction": true});
            skLineSegment(sketch, "E183.MirrorCS", {"start": v(-609.6, -1217.93) * mm, "end": v(-653.31, -1217.93) * mm, "construction": true});
            skLineSegment(sketch, "E184.MirrorCS", {"start": v(-881.35, -928.37) * mm, "end": v(-925.07, -928.37) * mm, "construction": true});
            skLineSegment(sketch, "E185.MirrorCS", {"start": v(-881.35, -824.23) * mm, "end": v(-925.07, -824.23) * mm, "construction": true});
            skLineSegment(sketch, "E186.MirrorCS", {"start": v(-653.31, -928.37) * mm, "end": v(-609.6, -928.37) * mm, "construction": true});
            skLineSegment(sketch, "E187.MirrorCS", {"start": v(-653.31, -824.23) * mm, "end": v(-609.6, -824.23) * mm, "construction": true});
            skPoint(sketch, "E188.endSnap0", {"position": v(-903.21, -1322.07) * mm});
            skLineSegment(sketch, "E189.bottom", {"start": v(-940.94, -824.23) * mm, "end": v(-915.54, -824.23) * mm});
            skLineSegment(sketch, "E189.top", {"start": v(-940.94, -928.37) * mm, "end": v(-915.54, -928.37) * mm});
            skLineSegment(sketch, "E189.left", {"start": v(-940.94, -824.23) * mm, "end": v(-940.94, -928.37) * mm});
            skLineSegment(sketch, "E189.right", {"start": v(-915.54, -824.23) * mm, "end": v(-915.54, -928.37) * mm});
            skLineSegment(sketch, "E190.bottom", {"start": v(-940.94, -1004.57) * mm, "end": v(-922.9, -1004.57) * mm});
            skLineSegment(sketch, "E190.top", {"start": v(-940.94, -928.37) * mm, "end": v(-922.9, -928.37) * mm});
            skLineSegment(sketch, "E190.left", {"start": v(-940.94, -1004.57) * mm, "end": v(-940.94, -928.37) * mm});
            skLineSegment(sketch, "E190.right", {"start": v(-922.9, -1004.57) * mm, "end": v(-922.9, -928.37) * mm});
            skLineSegment(sketch, "E191", {"start": v(-940.94, -1270) * mm, "end": v(-593.72, -1270) * mm, "construction": true});
            skLineSegment(sketch, "E192", {"start": v(-767.33, -711.2) * mm, "end": v(-767.33, -1828.8) * mm, "construction": true});
            skLineSegment(sketch, "E193.MirrorCS", {"start": v(-593.73, -928.37) * mm, "end": v(-619.12, -928.37) * mm});
            skLineSegment(sketch, "E194.MirrorCS", {"start": v(-593.73, -928.37) * mm, "end": v(-611.76, -928.37) * mm});
            skLineSegment(sketch, "E195.MirrorCS", {"start": v(-593.73, -1004.57) * mm, "end": v(-611.76, -1004.57) * mm});
            skLineSegment(sketch, "E196.MirrorCS", {"start": v(-593.72, -824.23) * mm, "end": v(-619.12, -824.23) * mm});
            skLineSegment(sketch, "E197.MirrorCS", {"start": v(-611.76, -1004.57) * mm, "end": v(-611.76, -928.37) * mm});
            skLineSegment(sketch, "E198.MirrorCS", {"start": v(-593.72, -1004.57) * mm, "end": v(-593.72, -928.37) * mm});
            skLineSegment(sketch, "E199.MirrorCS", {"start": v(-593.72, -824.23) * mm, "end": v(-593.72, -928.37) * mm});
            skLineSegment(sketch, "E200.MirrorCS", {"start": v(-619.12, -824.23) * mm, "end": v(-619.12, -928.37) * mm});
            skLineSegment(sketch, "E201.MirrorCS", {"start": v(-940.94, -1611.63) * mm, "end": v(-915.54, -1611.63) * mm});
            skLineSegment(sketch, "E202.MirrorCS", {"start": v(-940.94, -1715.77) * mm, "end": v(-915.54, -1715.77) * mm});
            skLineSegment(sketch, "E203.MirrorCS", {"start": v(-940.94, -1715.77) * mm, "end": v(-940.94, -1611.63) * mm});
            skLineSegment(sketch, "E204.MirrorCS", {"start": v(-915.54, -1715.77) * mm, "end": v(-915.54, -1611.63) * mm});
            skLineSegment(sketch, "E205.MirrorCS", {"start": v(-593.73, -1611.63) * mm, "end": v(-619.12, -1611.63) * mm});
            skLineSegment(sketch, "E206.MirrorCS", {"start": v(-593.72, -1715.77) * mm, "end": v(-593.72, -1611.63) * mm});
            skLineSegment(sketch, "E207.MirrorCS", {"start": v(-619.12, -1715.77) * mm, "end": v(-619.12, -1611.63) * mm});
            skLineSegment(sketch, "E208.MirrorCS", {"start": v(-593.72, -1715.77) * mm, "end": v(-619.12, -1715.77) * mm});
            skLineSegment(sketch, "E209", {"start": v(-903.21, -1322.07) * mm, "end": v(-903.21, -1611.63) * mm, "construction": true});
            skLineSegment(sketch, "E210", {"start": v(-903.21, -1466.85) * mm, "end": v(-767.33, -1466.85) * mm, "construction": true});
            skLineSegment(sketch, "E211.MirrorCS", {"start": v(-940.94, -1322.07) * mm, "end": v(-915.54, -1322.07) * mm});
            skLineSegment(sketch, "E212.MirrorCS", {"start": v(-940.94, -1217.93) * mm, "end": v(-915.54, -1217.93) * mm});
            skLineSegment(sketch, "E213.MirrorCS", {"start": v(-940.94, -1217.93) * mm, "end": v(-940.94, -1322.07) * mm});
            skLineSegment(sketch, "E214.MirrorCS", {"start": v(-915.54, -1217.93) * mm, "end": v(-915.54, -1322.07) * mm});
            skLineSegment(sketch, "E215.bottom", {"start": v(-593.72, -1217.93) * mm, "end": v(-619.12, -1217.93) * mm});
            skLineSegment(sketch, "E215.top", {"start": v(-593.72, -1322.07) * mm, "end": v(-619.12, -1322.07) * mm});
            skLineSegment(sketch, "E215.left", {"start": v(-593.72, -1217.93) * mm, "end": v(-593.72, -1322.07) * mm});
            skLineSegment(sketch, "E215.right", {"start": v(-619.12, -1217.93) * mm, "end": v(-619.12, -1322.07) * mm});
            skLineSegment(sketch, "E216.bottom", {"start": v(-593.72, -1398.27) * mm, "end": v(-611.76, -1398.27) * mm});
            skLineSegment(sketch, "E216.top", {"start": v(-593.72, -1322.07) * mm, "end": v(-611.76, -1322.07) * mm});
            skLineSegment(sketch, "E216.left", {"start": v(-593.72, -1398.27) * mm, "end": v(-593.72, -1322.07) * mm});
            skLineSegment(sketch, "E216.right", {"start": v(-611.76, -1398.27) * mm, "end": v(-611.76, -1322.07) * mm});
            skLineSegment(sketch, "E217.bottom", {"start": v(-441.32, -928.37) * mm, "end": v(-415.92, -928.37) * mm});
            skLineSegment(sketch, "E217.top", {"start": v(-441.32, -1791.97) * mm, "end": v(-415.92, -1791.97) * mm});
            skLineSegment(sketch, "E217.left", {"start": v(-441.32, -928.37) * mm, "end": v(-441.32, -1791.97) * mm});
            skLineSegment(sketch, "E217.right", {"start": v(-415.92, -928.37) * mm, "end": v(-415.92, -1791.97) * mm});
            skLineSegment(sketch, "E218.bottom", {"start": v(-940.94, -1398.27) * mm, "end": v(-922.9, -1398.27) * mm});
            skLineSegment(sketch, "E218.top", {"start": v(-940.94, -1322.07) * mm, "end": v(-922.9, -1322.07) * mm});
            skLineSegment(sketch, "E218.left", {"start": v(-940.94, -1398.27) * mm, "end": v(-940.94, -1322.07) * mm});
            skLineSegment(sketch, "E218.right", {"start": v(-922.9, -1398.27) * mm, "end": v(-922.9, -1322.07) * mm});
            skLineSegment(sketch, "E219.bottom", {"start": v(-940.94, -1791.97) * mm, "end": v(-922.9, -1791.97) * mm});
            skLineSegment(sketch, "E219.top", {"start": v(-940.94, -1715.77) * mm, "end": v(-922.9, -1715.77) * mm});
            skLineSegment(sketch, "E219.left", {"start": v(-940.94, -1791.97) * mm, "end": v(-940.94, -1715.77) * mm});
            skLineSegment(sketch, "E219.right", {"start": v(-922.9, -1791.97) * mm, "end": v(-922.9, -1715.77) * mm});
            skLineSegment(sketch, "E220.MirrorCS", {"start": v(-593.72, -1791.97) * mm, "end": v(-611.76, -1791.97) * mm});
            skLineSegment(sketch, "E221.MirrorCS", {"start": v(-593.72, -1791.97) * mm, "end": v(-593.72, -1715.77) * mm});
            skLineSegment(sketch, "E222.MirrorCS", {"start": v(-593.72, -1715.77) * mm, "end": v(-611.76, -1715.77) * mm});
            skLineSegment(sketch, "E223.MirrorCS", {"start": v(-611.76, -1791.97) * mm, "end": v(-611.76, -1715.77) * mm});
            skLineSegment(sketch, "E224", {"start": v(-441.32, -928.37) * mm, "end": v(-491.1, -928.37) * mm});
            skLineSegment(sketch, "E225", {"start": v(-491.1, -928.37) * mm, "end": v(-491.1, -1004.57) * mm});
            skLineSegment(sketch, "E226", {"start": v(-491.1, -1004.57) * mm, "end": v(-441.32, -1004.57) * mm});
            skLineSegment(sketch, "E227", {"start": v(-441.32, -1322.07) * mm, "end": v(-491.1, -1322.07) * mm});
            skLineSegment(sketch, "E228", {"start": v(-491.1, -1322.07) * mm, "end": v(-491.1, -1398.27) * mm});
            skLineSegment(sketch, "E229", {"start": v(-491.1, -1398.27) * mm, "end": v(-441.32, -1398.27) * mm});
            skLineSegment(sketch, "E230", {"start": v(-441.32, -1791.97) * mm, "end": v(-491.1, -1791.97) * mm});
            skLineSegment(sketch, "E231", {"start": v(-491.1, -1791.97) * mm, "end": v(-491.1, -1715.77) * mm});
            skLineSegment(sketch, "E232", {"start": v(-491.1, -1715.77) * mm, "end": v(-441.32, -1715.77) * mm});
            skLineSegment(sketch, "E233.MirrorCS", {"start": v(-776.35, -711.2) * mm, "end": v(-758.32, -711.2) * mm});
            skLineSegment(sketch, "E234.MirrorCS", {"start": v(-776.35, -711.2) * mm, "end": v(-776.35, -729.23) * mm});
            skLineSegment(sketch, "E235.MirrorCS", {"start": v(-827.15, -711.2) * mm, "end": v(-827.15, -729.23) * mm});
            skLineSegment(sketch, "E236.MirrorCS", {"start": v(-707.52, -711.2) * mm, "end": v(-707.52, -729.23) * mm});
            skLineSegment(sketch, "E237.MirrorCS", {"start": v(-758.32, -711.2) * mm, "end": v(-758.32, -729.23) * mm});
            skLineSegment(sketch, "E238.MirrorCS", {"start": v(-758.32, -729.23) * mm, "end": v(-707.52, -729.23) * mm});
            skLineSegment(sketch, "E239.MirrorCS", {"start": v(-776.35, -787.4) * mm, "end": v(-776.35, -711.2) * mm});
            skLineSegment(sketch, "E240.MirrorCS", {"start": v(-776.35, -729.23) * mm, "end": v(-827.15, -729.23) * mm});
            skLineSegment(sketch, "E241.MirrorCS", {"start": v(-776.35, -711.2) * mm, "end": v(-827.15, -711.2) * mm});
            skLineSegment(sketch, "E242.MirrorCS", {"start": v(-758.32, -711.2) * mm, "end": v(-707.52, -711.2) * mm});
            skLineSegment(sketch, "E243.MirrorCS", {"start": v(-758.32, -787.4) * mm, "end": v(-758.32, -711.2) * mm});
            skLineSegment(sketch, "E244.MirrorCS", {"start": v(-776.35, -787.4) * mm, "end": v(-758.32, -787.4) * mm});
            skLineSegment(sketch, "E245.MirrorCS", {"start": v(-758.32, -1828.8) * mm, "end": v(-758.32, -1810.77) * mm});
            skLineSegment(sketch, "E246.MirrorCS", {"start": v(-776.35, -1828.8) * mm, "end": v(-758.32, -1828.8) * mm});
            skLineSegment(sketch, "E247.MirrorCS", {"start": v(-776.35, -1828.8) * mm, "end": v(-776.35, -1810.77) * mm});
            skLineSegment(sketch, "E248.MirrorCS", {"start": v(-776.35, -1574.8) * mm, "end": v(-758.32, -1574.8) * mm});
            skLineSegment(sketch, "E249.MirrorCS", {"start": v(-776.35, -1752.6) * mm, "end": v(-758.32, -1752.6) * mm});
            skLineSegment(sketch, "E250.MirrorCS", {"start": v(-827.15, -1828.8) * mm, "end": v(-827.15, -1810.77) * mm});
            skLineSegment(sketch, "E251.MirrorCS", {"start": v(-758.32, -1828.8) * mm, "end": v(-758.32, -1752.6) * mm});
            skLineSegment(sketch, "E252.MirrorCS", {"start": v(-758.32, -1828.8) * mm, "end": v(-707.52, -1828.8) * mm});
            skLineSegment(sketch, "E253.MirrorCS", {"start": v(-758.32, -1810.77) * mm, "end": v(-707.52, -1810.77) * mm});
            skLineSegment(sketch, "E254.MirrorCS", {"start": v(-776.35, -1358.9) * mm, "end": v(-758.32, -1358.9) * mm});
            skLineSegment(sketch, "E255.MirrorCS", {"start": v(-707.52, -1828.8) * mm, "end": v(-707.52, -1810.77) * mm});
            skLineSegment(sketch, "E256.MirrorCS", {"start": v(-776.35, -1181.1) * mm, "end": v(-758.32, -1181.1) * mm});
            skLineSegment(sketch, "E257.MirrorCS", {"start": v(-776.35, -1828.8) * mm, "end": v(-776.35, -1752.6) * mm});
            skLineSegment(sketch, "E258.MirrorCS", {"start": v(-776.35, -1828.8) * mm, "end": v(-827.15, -1828.8) * mm});
            skLineSegment(sketch, "E259.MirrorCS", {"start": v(-776.35, -965.2) * mm, "end": v(-758.32, -965.2) * mm});
            skLineSegment(sketch, "E260.MirrorCS", {"start": v(-776.35, -1810.77) * mm, "end": v(-827.15, -1810.77) * mm});
            skPoint(sketch, "E261.MirrorP", {"position": v(-758.32, -1663.7) * mm});
            skLineSegment(sketch, "E262.MirrorCS", {"start": v(-776.35, -1574.8) * mm, "end": v(-776.35, -1358.9) * mm});
            skLineSegment(sketch, "E263.MirrorCS", {"start": v(-758.32, -1574.8) * mm, "end": v(-758.32, -1358.9) * mm});
            skLineSegment(sketch, "E264.MirrorCS", {"start": v(-758.32, -1181.1) * mm, "end": v(-758.32, -965.2) * mm});
            skLineSegment(sketch, "E265.MirrorCS", {"start": v(-776.35, -1181.1) * mm, "end": v(-776.35, -965.2) * mm});
            skLineSegment(sketch, "E266.MirrorCS", {"start": v(-758.32, -1752.6) * mm, "end": v(-758.32, -1574.8) * mm, "construction": true});
            skPoint(sketch, "E267.MirrorP", {"position": v(-767.33, -1828.8) * mm});
            skLineSegment(sketch, "E268", {"start": v(-1001.27, -558.8) * mm, "end": v(-1001.27, 558.8) * mm, "construction": true});
            skLineSegment(sketch, "E269.MirrorCS", {"start": v(-1226.18, 558.8) * mm, "end": v(-1226.18, 540.77) * mm});
            skLineSegment(sketch, "E270.MirrorCS", {"start": v(-1226.18, 558.8) * mm, "end": v(-1226.18, 482.6) * mm});
            skLineSegment(sketch, "E271.MirrorCS", {"start": v(-1226.18, 540.77) * mm, "end": v(-1175.38, 540.77) * mm});
            skLineSegment(sketch, "E272.MirrorCS", {"start": v(-1175.38, 558.8) * mm, "end": v(-1175.38, 540.77) * mm});
            skPoint(sketch, "E273.MirrorP", {"position": v(-1235.2, 558.8) * mm});
            skLineSegment(sketch, "E274.MirrorCS", {"start": v(-1226.18, 558.8) * mm, "end": v(-1175.38, 558.8) * mm});
            skLineSegment(sketch, "E275.MirrorCS", {"start": v(-1244.22, 558.8) * mm, "end": v(-1244.22, 482.6) * mm});
            skLineSegment(sketch, "E276.MirrorCS", {"start": v(-1226.18, 482.6) * mm, "end": v(-1244.22, 482.6) * mm});
            skLineSegment(sketch, "E277.MirrorCS", {"start": v(-1226.18, 558.8) * mm, "end": v(-1244.22, 558.8) * mm});
            skLineSegment(sketch, "E278.MirrorCS", {"start": v(-1244.22, 304.8) * mm, "end": v(-1244.22, 88.9) * mm});
            skLineSegment(sketch, "E279.MirrorCS", {"start": v(-1226.18, 304.8) * mm, "end": v(-1226.18, 88.9) * mm});
            skLineSegment(sketch, "E280.MirrorCS", {"start": v(-1226.18, 88.9) * mm, "end": v(-1244.22, 88.9) * mm});
            skLineSegment(sketch, "E281.MirrorCS", {"start": v(-1226.18, 304.8) * mm, "end": v(-1244.22, 304.8) * mm});
            skLineSegment(sketch, "E282.MirrorCS", {"start": v(-1226.18, -88.9) * mm, "end": v(-1244.22, -88.9) * mm});
            skLineSegment(sketch, "E283.MirrorCS", {"start": v(-1226.18, -558.8) * mm, "end": v(-1175.38, -558.8) * mm});
            skPoint(sketch, "E284.MirrorP", {"position": v(-1235.2, -558.8) * mm});
            skLineSegment(sketch, "E285.MirrorCS", {"start": v(-1226.18, -558.8) * mm, "end": v(-1226.18, -540.77) * mm});
            skLineSegment(sketch, "E286.MirrorCS", {"start": v(-1226.18, -540.77) * mm, "end": v(-1175.38, -540.77) * mm});
            skLineSegment(sketch, "E287.MirrorCS", {"start": v(-1175.38, -558.8) * mm, "end": v(-1175.38, -540.77) * mm});
            skLineSegment(sketch, "E288.MirrorCS", {"start": v(-1226.18, -558.8) * mm, "end": v(-1244.22, -558.8) * mm});
            skLineSegment(sketch, "E289.MirrorCS", {"start": v(-1226.18, -482.6) * mm, "end": v(-1226.18, -558.8) * mm});
            skLineSegment(sketch, "E290.MirrorCS", {"start": v(-1226.18, -482.6) * mm, "end": v(-1244.22, -482.6) * mm});
            skLineSegment(sketch, "E291.MirrorCS", {"start": v(-1244.22, -482.6) * mm, "end": v(-1244.22, -558.8) * mm});
            skLineSegment(sketch, "E292.MirrorCS", {"start": v(-1226.18, -88.9) * mm, "end": v(-1226.18, -304.8) * mm});
            skLineSegment(sketch, "E293.MirrorCS", {"start": v(-1244.22, -88.9) * mm, "end": v(-1244.22, -304.8) * mm});
            skLineSegment(sketch, "E294.MirrorCS", {"start": v(-1226.18, -304.8) * mm, "end": v(-1244.22, -304.8) * mm});
            skLineSegment(sketch, "E295", {"start": v(-1086.48, 558.8) * mm, "end": v(-1086.48, -558.8) * mm});
            skLineSegment(sketch, "E296", {"start": v(-1086.48, 558.8) * mm, "end": v(-1244.22, 558.8) * mm});
            skLineSegment(sketch, "E297", {"start": v(-1244.22, -558.8) * mm, "end": v(-1086.48, -558.8) * mm});
            skLineSegment(sketch, "E298", {"start": v(-1244.22, -558.8) * mm, "end": v(-1244.22, 558.8) * mm});
            skLineSegment(sketch, "E299.MirrorCS", {"start": v(-1226.18, -711.2) * mm, "end": v(-1244.22, -711.2) * mm});
            skLineSegment(sketch, "E300.MirrorCS", {"start": v(-1226.18, -711.2) * mm, "end": v(-1226.18, -729.23) * mm});
            skLineSegment(sketch, "E301.MirrorCS", {"start": v(-1226.18, -1828.8) * mm, "end": v(-1244.22, -1828.8) * mm});
            skLineSegment(sketch, "E302.MirrorCS", {"start": v(-1226.18, -1828.8) * mm, "end": v(-1226.18, -1810.77) * mm});
            skLineSegment(sketch, "E303.MirrorCS", {"start": v(-1226.18, -711.2) * mm, "end": v(-1175.38, -711.2) * mm});
            skLineSegment(sketch, "E304.MirrorCS", {"start": v(-1226.18, -787.4) * mm, "end": v(-1226.18, -711.2) * mm});
            skLineSegment(sketch, "E305.MirrorCS", {"start": v(-1175.38, -711.2) * mm, "end": v(-1175.38, -729.23) * mm});
            skLineSegment(sketch, "E306.MirrorCS", {"start": v(-1226.18, -729.23) * mm, "end": v(-1175.38, -729.23) * mm});
            skLineSegment(sketch, "E307.MirrorCS", {"start": v(-1226.18, -1828.8) * mm, "end": v(-1175.38, -1828.8) * mm});
            skLineSegment(sketch, "E308.MirrorCS", {"start": v(-1244.22, -787.4) * mm, "end": v(-1244.22, -711.2) * mm});
            skLineSegment(sketch, "E309.MirrorCS", {"start": v(-1175.38, -1828.8) * mm, "end": v(-1175.38, -1810.77) * mm});
            skLineSegment(sketch, "E310.MirrorCS", {"start": v(-1226.18, -787.4) * mm, "end": v(-1244.22, -787.4) * mm});
            skLineSegment(sketch, "E311.MirrorCS", {"start": v(-1226.18, -1810.77) * mm, "end": v(-1175.38, -1810.77) * mm});
            skLineSegment(sketch, "E312.MirrorCS", {"start": v(-1226.18, -1828.8) * mm, "end": v(-1226.18, -1752.6) * mm});
            skLineSegment(sketch, "E313.MirrorCS", {"start": v(-1226.18, -965.2) * mm, "end": v(-1244.22, -965.2) * mm});
            skLineSegment(sketch, "E314.MirrorCS", {"start": v(-1226.18, -1181.1) * mm, "end": v(-1244.22, -1181.1) * mm});
            skLineSegment(sketch, "E315.MirrorCS", {"start": v(-1226.18, -1752.6) * mm, "end": v(-1244.22, -1752.6) * mm});
            skLineSegment(sketch, "E316.MirrorCS", {"start": v(-1226.18, -1574.8) * mm, "end": v(-1244.22, -1574.8) * mm});
            skLineSegment(sketch, "E317.MirrorCS", {"start": v(-1244.22, -711.2) * mm, "end": v(-1086.48, -711.2) * mm});
            skLineSegment(sketch, "E318.MirrorCS", {"start": v(-1226.18, -1358.9) * mm, "end": v(-1244.22, -1358.9) * mm});
            skLineSegment(sketch, "E319.MirrorCS", {"start": v(-1086.48, -1828.8) * mm, "end": v(-1244.22, -1828.8) * mm});
            skLineSegment(sketch, "E320.MirrorCS", {"start": v(-1244.22, -1828.8) * mm, "end": v(-1244.22, -1752.6) * mm});
            skLineSegment(sketch, "E321.MirrorCS", {"start": v(-1244.22, -1574.8) * mm, "end": v(-1244.22, -1358.9) * mm});
            skLineSegment(sketch, "E322.MirrorCS", {"start": v(-1086.48, -1828.8) * mm, "end": v(-1086.48, -711.2) * mm});
            skPoint(sketch, "E323.MirrorP", {"position": v(-1235.2, -711.2) * mm});
            skPoint(sketch, "E324.MirrorP", {"position": v(-1235.2, -1828.8) * mm});
            skLineSegment(sketch, "E325.MirrorCS", {"start": v(-1244.22, -1181.1) * mm, "end": v(-1244.22, -965.2) * mm});
            skLineSegment(sketch, "E326.MirrorCS", {"start": v(-1244.22, -711.2) * mm, "end": v(-1244.22, -1828.8) * mm});
            skLineSegment(sketch, "E327.MirrorCS", {"start": v(-1226.18, -1574.8) * mm, "end": v(-1226.18, -1358.9) * mm});
            skLineSegment(sketch, "E328.MirrorCS", {"start": v(-1226.18, -1181.1) * mm, "end": v(-1226.18, -965.2) * mm});
            skLineSegment(sketch, "E329.bottom", {"start": v(-1086.48, -824.23) * mm, "end": v(-1061.08, -824.23) * mm});
            skLineSegment(sketch, "E329.top", {"start": v(-1086.48, -928.37) * mm, "end": v(-1061.08, -928.37) * mm});
            skLineSegment(sketch, "E329.left", {"start": v(-1086.48, -824.23) * mm, "end": v(-1086.48, -928.37) * mm});
            skLineSegment(sketch, "E329.right", {"start": v(-1061.08, -824.23) * mm, "end": v(-1061.08, -928.37) * mm});
            skPoint(sketch, "E330.firstSnap0", {"position": v(-1086.48, -1270) * mm});
            skLineSegment(sketch, "E330.bottom", {"start": v(-1086.48, -1322.07) * mm, "end": v(-1061.08, -1322.07) * mm});
            skLineSegment(sketch, "E330.top", {"start": v(-1086.48, -1217.93) * mm, "end": v(-1061.08, -1217.93) * mm});
            skLineSegment(sketch, "E330.left", {"start": v(-1086.48, -1322.07) * mm, "end": v(-1086.48, -1217.93) * mm});
            skLineSegment(sketch, "E330.right", {"start": v(-1061.08, -1322.07) * mm, "end": v(-1061.08, -1217.93) * mm});
            skLineSegment(sketch, "E331.bottom", {"start": v(-1086.48, -1715.77) * mm, "end": v(-1061.08, -1715.77) * mm});
            skLineSegment(sketch, "E331.top", {"start": v(-1086.48, -1611.63) * mm, "end": v(-1061.08, -1611.63) * mm});
            skLineSegment(sketch, "E331.left", {"start": v(-1086.48, -1715.77) * mm, "end": v(-1086.48, -1611.63) * mm});
            skLineSegment(sketch, "E331.right", {"start": v(-1061.08, -1715.77) * mm, "end": v(-1061.08, -1611.63) * mm});
            skLineSegment(sketch, "E332.bottom", {"start": v(-1086.48, -445.77) * mm, "end": v(-1130.2, -445.77) * mm});
            skLineSegment(sketch, "E332.top", {"start": v(-1086.48, -341.63) * mm, "end": v(-1130.2, -341.63) * mm});
            skLineSegment(sketch, "E332.left", {"start": v(-1086.48, -445.77) * mm, "end": v(-1086.48, -341.63) * mm});
            skLineSegment(sketch, "E332.right", {"start": v(-1130.2, -445.77) * mm, "end": v(-1130.2, -341.63) * mm});
            skLineSegment(sketch, "E333.bottom", {"start": v(-1086.48, -52.07) * mm, "end": v(-1130.2, -52.07) * mm});
            skLineSegment(sketch, "E333.top", {"start": v(-1086.48, 52.07) * mm, "end": v(-1130.2, 52.07) * mm});
            skLineSegment(sketch, "E333.left", {"start": v(-1086.48, -52.07) * mm, "end": v(-1086.48, 52.07) * mm});
            skLineSegment(sketch, "E333.right", {"start": v(-1130.2, -52.07) * mm, "end": v(-1130.2, 52.07) * mm});
            skLineSegment(sketch, "E334.bottom", {"start": v(-1086.48, 341.63) * mm, "end": v(-1130.2, 341.63) * mm});
            skLineSegment(sketch, "E334.top", {"start": v(-1086.48, 445.77) * mm, "end": v(-1130.2, 445.77) * mm});
            skLineSegment(sketch, "E334.left", {"start": v(-1086.48, 341.63) * mm, "end": v(-1086.48, 445.77) * mm});
            skLineSegment(sketch, "E334.right", {"start": v(-1130.2, 341.63) * mm, "end": v(-1130.2, 445.77) * mm});
            skSolve(sketch);
        }
        {
            var Q0;
            {var subQ1=sQuery(id+"F1.wireOp",EDGE,"E60.bottom");Q0=makeQuery(id+"F1.imprint","IMPRINT",FACE,{"disambiguationData":[TD([[makeQuery(id+"F1.imprint","IMPRINT",EDGE,{"derivedFrom":subQ1}),-1.0]])]});}
            var Q1;
            Q1=makeQuery(id+"F1.imprint","IMPRINT",FACE,{"disambiguationData":[TD([[makeQuery(id+"F1.imprint","IMPRINT",EDGE,{"derivedFrom":sQuery(id+"F1.wireOp",EDGE,"E61.bottom")}),-1.0]])]});
            var Q2;
            Q2=makeQuery(id+"F1.imprint","IMPRINT",FACE,{"disambiguationData":[TD([[makeQuery(id+"F1.imprint","IMPRINT",EDGE,{"derivedFrom":sQuery(id+"F1.wireOp",EDGE,"E62.bottom")}),1.0]])]});
            var Q3;
            Q3=makeQuery(id+"F1.imprint","IMPRINT",FACE,{"disambiguationData":[TD([[makeQuery(id+"F1.imprint","IMPRINT",EDGE,{"derivedFrom":sQuery(id+"F1.wireOp",EDGE,"E70.MirrorCS")}),1.0]])]});
            var Q4;
            Q4=makeQuery(id+"F1.imprint","IMPRINT",FACE,{"disambiguationData":[TD([[makeQuery(id+"F1.imprint","IMPRINT",EDGE,{"derivedFrom":sQuery(id+"F1.wireOp",EDGE,"E74.MirrorCS")}),1.0]])]});
            var Q5;
            {var subQ33=sQuery(id+"F1.wireOp",EDGE,"E1.bottom");Q5=makeQuery(id+"F1.imprint","IMPRINT",FACE,{"disambiguationData":[TD([[makeQuery(id+"F1.imprint","IMPRINT",EDGE,{"derivedFrom":subQ33}),1.0]])]});}
            var Q6;
            {var subQ6=sQuery(id+"F1.wireOp",EDGE,"E43.left");Q6=makeQuery(id+"F1.imprint","IMPRINT",FACE,{"disambiguationData":[TD([[makeQuery(id+"F1.imprint","IMPRINT",EDGE,{"derivedFrom":subQ6}),1.0]])]});}
            var Q7;
            {var subQ3=sQuery(id+"F1.wireOp",EDGE,"15a585a5-c292-47de-8cfe-40bc0ff959e20.MirrorCS");Q7=makeQuery(id+"F1.imprint","IMPRINT",FACE,{"disambiguationData":[TD([[makeQuery(id+"F1.imprint","IMPRINT",EDGE,{"derivedFrom":subQ3}),1.0]])]});}
            var Q8;
            {var subQ0=sQuery(id+"F1.wireOp",EDGE,"E94.MirrorCS");Q8=makeQuery(id+"F1.imprint","IMPRINT",FACE,{"disambiguationData":[TD([[makeQuery(id+"F1.imprint","IMPRINT",EDGE,{"derivedFrom":subQ0}),1.0]])]});}
            var Q9;
            {var subQ0=sQuery(id+"F1.wireOp",EDGE,"E100.MirrorCS");Q9=makeQuery(id+"F1.imprint","IMPRINT",FACE,{"disambiguationData":[TD([[makeQuery(id+"F1.imprint","IMPRINT",EDGE,{"derivedFrom":subQ0}),-1.0]])]});}
            var Q10;
            {var subQ10=sQuery(id+"F1.wireOp",EDGE,"E173.bottom");Q10=makeQuery(id+"F1.imprint","IMPRINT",FACE,{"disambiguationData":[TD([[makeQuery(id+"F1.imprint","IMPRINT",EDGE,{"derivedFrom":subQ10}),-1.0]])]});}
            var Q11;
            {var subQ0=sQuery(id+"F1.wireOp",EDGE,"vC60dyBu-nMOn-iXCW-ycnC-LK4FzoJF3nVa");Q11=makeQuery(id+"F1.imprint","IMPRINT",FACE,{"disambiguationData":[TD([[makeQuery(id+"F1.imprint","IMPRINT",EDGE,{"derivedFrom":subQ0}),-1.0]])]});}
            var Q12;
            {var subQ0=sQuery(id+"F1.wireOp",EDGE,"E227");Q12=makeQuery(id+"F1.imprint","IMPRINT",FACE,{"disambiguationData":[TD([[makeQuery(id+"F1.imprint","IMPRINT",EDGE,{"derivedFrom":subQ0}),1.0]])]});}
            var Q13;
            {var subQ0=sQuery(id+"F1.wireOp",EDGE,"E230");Q13=makeQuery(id+"F1.imprint","IMPRINT",FACE,{"disambiguationData":[TD([[makeQuery(id+"F1.imprint","IMPRINT",EDGE,{"derivedFrom":subQ0}),-1.0]])]});}
            var Q14;
            {var subQ3=sQuery(id+"F1.wireOp",EDGE,"E217.bottom");Q14=makeQuery(id+"F1.imprint","IMPRINT",FACE,{"disambiguationData":[TD([[makeQuery(id+"F1.imprint","IMPRINT",EDGE,{"derivedFrom":subQ3}),-1.0]])]});}
            var Q15;
            {var subQ0=sQuery(id+"F1.wireOp",EDGE,"E224");Q15=makeQuery(id+"F1.imprint","IMPRINT",FACE,{"disambiguationData":[TD([[makeQuery(id+"F1.imprint","IMPRINT",EDGE,{"derivedFrom":subQ0}),1.0]])]});}
            var Q16;
            {var subQ26=sQuery(id+"F1.wireOp",EDGE,"E271.MirrorCS");Q16=makeQuery(id+"F1.imprint","IMPRINT",FACE,{"disambiguationData":[TD([[makeQuery(id+"F1.imprint","IMPRINT",EDGE,{"derivedFrom":subQ26}),-1.0]])]});}
            var Q17;
            Q17=makeQuery(id+"F1.imprint","IMPRINT",FACE,{"disambiguationData":[TD([[makeQuery(id+"F1.imprint","IMPRINT",EDGE,{"derivedFrom":sQuery(id+"F1.wireOp",EDGE,"E329.bottom")}),-1.0]])]});
            var Q18;
            Q18=makeQuery(id+"F1.imprint","IMPRINT",FACE,{"disambiguationData":[TD([[makeQuery(id+"F1.imprint","IMPRINT",EDGE,{"derivedFrom":sQuery(id+"F1.wireOp",EDGE,"E331.bottom")}),1.0]])]});
            var Q19;
            Q19=makeQuery(id+"F1.imprint","IMPRINT",FACE,{"disambiguationData":[TD([[makeQuery(id+"F1.imprint","IMPRINT",EDGE,{"derivedFrom":sQuery(id+"F1.wireOp",EDGE,"E330.bottom")}),1.0]])]});
            var Q20;
            {var subQ15=sQuery(id+"F1.wireOp",EDGE,"E305.MirrorCS");Q20=makeQuery(id+"F1.imprint","IMPRINT",FACE,{"disambiguationData":[TD([[makeQuery(id+"F1.imprint","IMPRINT",EDGE,{"derivedFrom":subQ15}),1.0]])]});}
            extrude(context, id + "F2", {"entities" : qUnion([Q0, Q1, Q2, Q3, Q4, Q5, Q6, Q7, Q8, Q9, Q10, Q11, Q12, Q13, Q14, Q15, Q16, Q17, Q18, Q19, Q20]), "depth" : (getVariable(context, 'ply34')) * mm});
        }
        {
            var Q0;
            {var subQ6=sQuery(id+"F1.wireOp",EDGE,"E157.bottom");Q0=makeQuery(id+"F1.imprint","IMPRINT",FACE,{"disambiguationData":[TD([[makeQuery(id+"F1.imprint","IMPRINT",EDGE,{"derivedFrom":subQ6}),-1.0]])]});}
            var Q1;
            {var subQ0=sQuery(id+"F1.wireOp",EDGE,"E163");Q1=makeQuery(id+"F1.imprint","IMPRINT",FACE,{"disambiguationData":[TD([[makeQuery(id+"F1.imprint","IMPRINT",EDGE,{"derivedFrom":subQ0}),-1.0]])]});}
            var Q2;
            {var subQ0=sQuery(id+"F1.wireOp",EDGE,"E160");Q2=makeQuery(id+"F1.imprint","IMPRINT",FACE,{"disambiguationData":[TD([[makeQuery(id+"F1.imprint","IMPRINT",EDGE,{"derivedFrom":subQ0}),-1.0]])]});}
            var Q3;
            {var subQ0=sQuery(id+"F1.wireOp",EDGE,"E166");Q3=makeQuery(id+"F1.imprint","IMPRINT",FACE,{"disambiguationData":[TD([[makeQuery(id+"F1.imprint","IMPRINT",EDGE,{"derivedFrom":subQ0}),-1.0]])]});}
            var Q4;
            {var subQ0=sQuery(id+"F1.wireOp",EDGE,"E169");Q4=makeQuery(id+"F1.imprint","IMPRINT",FACE,{"disambiguationData":[TD([[makeQuery(id+"F1.imprint","IMPRINT",EDGE,{"derivedFrom":subQ0}),-1.0]])]});}
            extrude(context, id + "F3", {"entities" : qUnion([Q0, Q1, Q2, Q3, Q4]), "depth" : 12.2 * mm});
        }
        {
            var Q0;
            Q0=makeQuery(id+"F1.imprint","IMPRINT",FACE,{"disambiguationData":[TD([[makeQuery(id+"F1.imprint","IMPRINT",EDGE,{"derivedFrom":sQuery(id+"F1.wireOp",EDGE,"c5a33fef-cf20-4e9f-8e37-3778fd242a644.MirrorCS")}),1.0]])]});
            var Q1;
            Q1=makeQuery(id+"F1.imprint","IMPRINT",FACE,{"disambiguationData":[TD([[makeQuery(id+"F1.imprint","IMPRINT",EDGE,{"derivedFrom":sQuery(id+"F1.wireOp",EDGE,"E120.MirrorCS")}),1.0]])]});
            var Q2;
            Q2=makeQuery(id+"F1.imprint","IMPRINT",FACE,{"disambiguationData":[TD([[makeQuery(id+"F1.imprint","IMPRINT",EDGE,{"derivedFrom":sQuery(id+"F1.wireOp",EDGE,"E112.bottom")}),1.0]])]});
            var Q3;
            Q3=makeQuery(id+"F1.imprint","IMPRINT",FACE,{"disambiguationData":[TD([[makeQuery(id+"F1.imprint","IMPRINT",EDGE,{"derivedFrom":sQuery(id+"F1.wireOp",EDGE,"E109.bottom")}),1.0]])]});
            var Q4;
            Q4=makeQuery(id+"F1.imprint","IMPRINT",FACE,{"disambiguationData":[TD([[makeQuery(id+"F1.imprint","IMPRINT",EDGE,{"derivedFrom":sQuery(id+"F1.wireOp",EDGE,"E122.MirrorCS")}),1.0]])]});
            var Q5;
            Q5=makeQuery(id+"F1.imprint","IMPRINT",FACE,{"disambiguationData":[TD([[makeQuery(id+"F1.imprint","IMPRINT",EDGE,{"derivedFrom":sQuery(id+"F1.wireOp",EDGE,"c5a33fef-cf20-4e9f-8e37-3778fd242a642.MirrorCS")}),-1.0]])]});
            var Q6;
            Q6=makeQuery(id+"F1.imprint","IMPRINT",FACE,{"disambiguationData":[TD([[makeQuery(id+"F1.imprint","IMPRINT",EDGE,{"derivedFrom":sQuery(id+"F1.wireOp",EDGE,"c5a33fef-cf20-4e9f-8e37-3778fd242a640.MirrorCS")}),-1.0]])]});
            var Q7;
            Q7=makeQuery(id+"F1.imprint","IMPRINT",FACE,{"disambiguationData":[TD([[makeQuery(id+"F1.imprint","IMPRINT",EDGE,{"derivedFrom":sQuery(id+"F1.wireOp",EDGE,"E118.MirrorCS")}),-1.0]])]});
            var Q8;
            Q8=makeQuery(id+"F1.imprint","IMPRINT",FACE,{"disambiguationData":[TD([[makeQuery(id+"F1.imprint","IMPRINT",EDGE,{"derivedFrom":sQuery(id+"F1.wireOp",EDGE,"E113.MirrorCS")}),-1.0]])]});
            var Q9;
            Q9=makeQuery(id+"F1.imprint","IMPRINT",FACE,{"disambiguationData":[TD([[makeQuery(id+"F1.imprint","IMPRINT",EDGE,{"derivedFrom":sQuery(id+"F1.wireOp",EDGE,"E332.bottom")}),-1.0]])]});
            var Q10;
            Q10=makeQuery(id+"F1.imprint","IMPRINT",FACE,{"disambiguationData":[TD([[makeQuery(id+"F1.imprint","IMPRINT",EDGE,{"derivedFrom":sQuery(id+"F1.wireOp",EDGE,"E333.bottom")}),-1.0]])]});
            var Q11;
            Q11=makeQuery(id+"F1.imprint","IMPRINT",FACE,{"disambiguationData":[TD([[makeQuery(id+"F1.imprint","IMPRINT",EDGE,{"derivedFrom":sQuery(id+"F1.wireOp",EDGE,"E334.bottom")}),-1.0]])]});
            extrude(context, id + "F4", {"entities" : qUnion([Q0, Q1, Q2, Q3, Q4, Q5, Q6, Q7, Q8, Q9, Q10, Q11]), "operationType" : NewBodyOperationType.ADD, "depth" : (getVariable(context, 'ply34') - .129) * mm});
        }
    });
